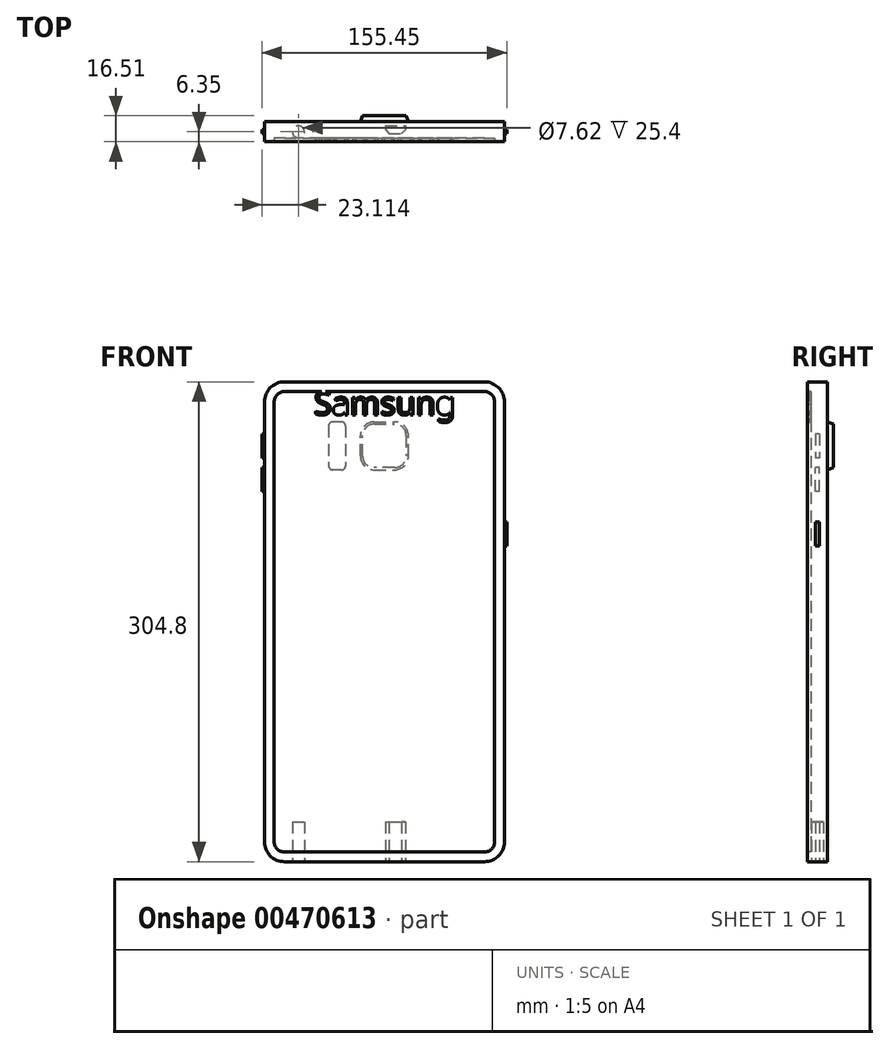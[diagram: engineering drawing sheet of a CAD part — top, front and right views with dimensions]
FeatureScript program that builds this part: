
annotation { "Feature Type Name" : "Feature", "Feature Type Description" : "" }
export const myFeature = defineFeature(function(context is Context, id is Id, definition is map)
    precondition{}
    {
        {
            var Q0;
            Q0=qCreatedBy(makeId("Front.planeOp"),FACE);
            var sketch = newSketch(context, id + "F0", { "sketchPlane" : qUnion([Q0])});
            skLineSegment(sketch, "E0.bottom", {"start": v(-70.4, 199.2) * mm, "end": v(56.6, 199.2) * mm});
            skLineSegment(sketch, "E0.top", {"start": v(-70.4, -105.6) * mm, "end": v(56.6, -105.6) * mm});
            skLineSegment(sketch, "E0.left", {"start": v(-83.1, 186.5) * mm, "end": v(-83.1, -92.9) * mm});
            skLineSegment(sketch, "E0.right", {"start": v(69.3, 186.5) * mm, "end": v(69.3, -92.9) * mm});
            skPoint(sketch, "E1.visualSharp", {"position": v(-83.1, 199.2) * mm});
            skArc(sketch, "E1.filletArc", {"start": v(-70.4, 199.2) * mm, "mid": v(-79.39, 195.48) * mm, "end": v(-83.1, 186.5) * mm});
            skPoint(sketch, "E2.visualSharp", {"position": v(69.3, 199.2) * mm});
            skArc(sketch, "E2.filletArc", {"start": v(69.3, 186.5) * mm, "mid": v(65.57, 195.48) * mm, "end": v(56.6, 199.2) * mm});
            skPoint(sketch, "E3.visualSharp", {"position": v(69.3, -105.6) * mm});
            skArc(sketch, "E3.filletArc", {"start": v(56.6, -105.6) * mm, "mid": v(65.57, -101.88) * mm, "end": v(69.3, -92.9) * mm});
            skPoint(sketch, "E4.visualSharp", {"position": v(-83.1, -105.6) * mm});
            skArc(sketch, "E4.filletArc", {"start": v(-83.1, -92.9) * mm, "mid": v(-79.39, -101.88) * mm, "end": v(-70.4, -105.6) * mm});
            skSolve(sketch);
        }
        {
            var Q0;
            Q0 = qSketchRegion(id + "F0", true);
            extrude(context, id + "F1", {"entities" : qUnion([Q0]), "depth" : 12.7 * mm});
        }
        {
            var Q0;
            Q0=makeQuery(id+"F1.opExtrude","SWEPT_FACE",FACE,{"disambiguationData":[OSD([sQuery(id+"F0.wireOp",EDGE,"E0.top")])]});
            var sketch = newSketch(context, id + "F2", { "sketchPlane" : qUnion([Q0])});
            skCircle(sketch, "E5", {"center": v(-61.52, 6.35) * mm, "radius": 3.81 * mm});
            skLineSegment(sketch, "E6.bottom", {"start": v(-6.35, 2.54) * mm, "end": v(6.35, 2.54) * mm});
            skLineSegment(sketch, "E6.top", {"start": v(-6.35, 7.62) * mm, "end": v(6.35, 7.62) * mm});
            skLineSegment(sketch, "E6.left", {"start": v(-6.35, 2.54) * mm, "end": v(-6.35, 7.62) * mm});
            skLineSegment(sketch, "E6.right", {"start": v(6.35, 2.54) * mm, "end": v(6.35, 7.62) * mm});
            skLineSegment(sketch, "E7", {"start": v(-6.35, 5.08) * mm, "end": v(-4.06, 7.62) * mm});
            skLineSegment(sketch, "E8.MirrorCS", {"start": v(6.35, 5.08) * mm, "end": v(4.06, 7.62) * mm});
            skLineSegment(sketch, "E9.0.0", {"start": v(-70.4, 0) * mm, "end": v(56.6, 0) * mm});
            skLineSegment(sketch, "E9.0.1", {"start": v(56.6, 0) * mm, "end": v(56.6, 12.7) * mm});
            skLineSegment(sketch, "E9.0.2", {"start": v(56.6, 12.7) * mm, "end": v(-70.4, 12.7) * mm});
            skLineSegment(sketch, "E9.0.3", {"start": v(-70.4, 12.7) * mm, "end": v(-70.4, 0) * mm});
            skSolve(sketch);
        }
        {
            var Q0;
            Q0=makeQuery(id+"F2.imprint","IMPRINT",FACE,{"disambiguationData":[TD([[makeQuery(id+"F2.imprint","IMPRINT",EDGE,{"derivedFrom":sQuery(id+"F2.wireOp",EDGE,"E5")}),1.0]])]});
            var Q1;
            {var subQ1=sQuery(id+"F2.wireOp",EDGE,"E6.bottom");Q1=makeQuery(id+"F2.imprint","IMPRINT",FACE,{"disambiguationData":[TD([[makeQuery(id+"F2.imprint","IMPRINT",EDGE,{"derivedFrom":subQ1}),1.0]])]});}
            extrude(context, id + "F3", {"entities" : qUnion([Q0, Q1]), "operationType" : NewBodyOperationType.REMOVE, "oppositeDirection" : true, "depth" : 25.4 * mm});
        }
        {
            var Q0;
            Q0=makeQuery(id+"F1.opExtrude","CAP_FACE",FACE,{"disambiguationData":[OSD([sQuery(id+"F0.wireOp",EDGE,"E0.bottom"),sQuery(id+"F0.wireOp",EDGE,"E0.top"),sQuery(id+"F0.wireOp",EDGE,"E0.left"),sQuery(id+"F0.wireOp",EDGE,"E0.right"),sQuery(id+"F0.wireOp",EDGE,"E1.filletArc"),sQuery(id+"F0.wireOp",EDGE,"E2.filletArc"),sQuery(id+"F0.wireOp",EDGE,"E3.filletArc"),sQuery(id+"F0.wireOp",EDGE,"E4.filletArc")])],"isStart":false});
            var sketch = newSketch(context, id + "F4", { "sketchPlane" : qUnion([Q0])});
            skLineSegment(sketch, "E10.0", {"start": v(-76.96, 186.5) * mm, "end": v(-76.96, -92.9) * mm});
            skArc(sketch, "E10.1", {"start": v(-70.4, 193.05) * mm, "mid": v(-75.04, 191.13) * mm, "end": v(-76.96, 186.5) * mm});
            skArc(sketch, "E10.2", {"start": v(-76.96, -92.9) * mm, "mid": v(-75.04, -97.54) * mm, "end": v(-70.4, -99.46) * mm});
            skLineSegment(sketch, "E10.3", {"start": v(56.6, 193.05) * mm, "end": v(-70.4, 193.05) * mm});
            skLineSegment(sketch, "E10.4", {"start": v(-70.4, -99.46) * mm, "end": v(56.6, -99.46) * mm});
            skArc(sketch, "E10.5", {"start": v(56.6, -99.46) * mm, "mid": v(61.23, -97.54) * mm, "end": v(63.15, -92.9) * mm});
            skLineSegment(sketch, "E10.6", {"start": v(63.15, -92.9) * mm, "end": v(63.15, 186.5) * mm});
            skArc(sketch, "E10.7", {"start": v(63.15, 186.5) * mm, "mid": v(61.23, 191.13) * mm, "end": v(56.6, 193.05) * mm});
            skText(sketch, "E11", { "text": "Samsung", "fontName": "NotoSans-Regular.ttf"});
            const initialGuessF4  = {"E11": [-0.05156, 0.17829, 1, 0, 0.01477]};
            skSetInitialGuess(sketch, initialGuessF4);
            skSolve(sketch);
        }
        {
            var Q0;
            Q0=makeQuery(id+"F4.imprint","IMPRINT",FACE,{"disambiguationData":[TD([[makeQuery(id+"F4.imprint","IMPRINT",EDGE,{"derivedFrom":sQuery(id+"F4.wireOp",EDGE,"E10.0")}),1.0]])]});
            extrude(context, id + "F5", {"entities" : qUnion([Q0]), "operationType" : NewBodyOperationType.REMOVE, "oppositeDirection" : true, "depth" : 2.3 * mm});
        }
        {
            var Q0;
            Q0=makeQuery(id+"F1.opExtrude","SWEPT_FACE",FACE,{"disambiguationData":[OSD([sQuery(id+"F0.wireOp",EDGE,"E0.left")])]});
            var sketch = newSketch(context, id + "F6", { "sketchPlane" : qUnion([Q0])});
            skLineSegment(sketch, "E12.bottom", {"start": v(5.08, 166.18) * mm, "end": v(7.62, 166.18) * mm});
            skLineSegment(sketch, "E12.top", {"start": v(5.08, 150.94) * mm, "end": v(7.62, 150.94) * mm});
            skLineSegment(sketch, "E12.left", {"start": v(5.08, 166.18) * mm, "end": v(5.08, 150.94) * mm});
            skLineSegment(sketch, "E12.right", {"start": v(7.62, 166.18) * mm, "end": v(7.62, 150.94) * mm});
            skLineSegment(sketch, "E13.MirrorCS", {"start": v(5.08, 129.47) * mm, "end": v(5.08, 144.7) * mm});
            skLineSegment(sketch, "E14.MirrorCS", {"start": v(7.62, 129.47) * mm, "end": v(7.62, 144.7) * mm});
            skLineSegment(sketch, "E15.MirrorCS", {"start": v(5.08, 144.7) * mm, "end": v(7.62, 144.7) * mm});
            skLineSegment(sketch, "E16.MirrorCS", {"start": v(5.08, 129.47) * mm, "end": v(7.62, 129.47) * mm});
            skSolve(sketch);
        }
        {
            var Q0;
            Q0=makeQuery(id+"F6.imprint","IMPRINT",FACE,{"disambiguationData":[TD([[makeQuery(id+"F6.imprint","IMPRINT",EDGE,{"derivedFrom":sQuery(id+"F6.wireOp",EDGE,"E12.bottom")}),-1.0]])]});
            var Q1;
            Q1=makeQuery(id+"F6.imprint","IMPRINT",FACE,{"disambiguationData":[TD([[makeQuery(id+"F6.imprint","IMPRINT",EDGE,{"derivedFrom":sQuery(id+"F6.wireOp",EDGE,"E13.MirrorCS")}),-1.0]])]});
            extrude(context, id + "F7", {"entities" : qUnion([Q0, Q1]), "operationType" : NewBodyOperationType.ADD, "depth" : 1.52 * mm});
        }
        {
            var Q0;
            Q0=makeQuery(id+"F1.opExtrude","SWEPT_FACE",FACE,{"disambiguationData":[OSD([sQuery(id+"F0.wireOp",EDGE,"E0.right")])]});
            var sketch = newSketch(context, id + "F8", { "sketchPlane" : qUnion([Q0])});
            skLineSegment(sketch, "E17.bottom", {"start": v(-7.62, 95.06) * mm, "end": v(-5.08, 95.06) * mm});
            skLineSegment(sketch, "E17.top", {"start": v(-7.62, 110.3) * mm, "end": v(-5.08, 110.3) * mm});
            skLineSegment(sketch, "E17.left", {"start": v(-7.62, 95.06) * mm, "end": v(-7.62, 110.3) * mm});
            skLineSegment(sketch, "E17.right", {"start": v(-5.08, 95.06) * mm, "end": v(-5.08, 110.3) * mm});
            skSolve(sketch);
        }
        {
            var Q0;
            Q0=makeQuery(id+"F8.imprint","IMPRINT",FACE,{"disambiguationData":[TD([[makeQuery(id+"F8.imprint","IMPRINT",EDGE,{"derivedFrom":sQuery(id+"F8.wireOp",EDGE,"E17.bottom")}),1.0]])]});
            extrude(context, id + "F9", {"entities" : qUnion([Q0]), "operationType" : NewBodyOperationType.ADD, "depth" : 1.52 * mm});
        }
        {
            var Q0;
            Q0=makeQuery(id+"F1.opExtrude","CAP_FACE",FACE,{"disambiguationData":[OSD([sQuery(id+"F0.wireOp",EDGE,"E0.bottom"),sQuery(id+"F0.wireOp",EDGE,"E0.top"),sQuery(id+"F0.wireOp",EDGE,"E0.left"),sQuery(id+"F0.wireOp",EDGE,"E0.right"),sQuery(id+"F0.wireOp",EDGE,"E1.filletArc"),sQuery(id+"F0.wireOp",EDGE,"E2.filletArc"),sQuery(id+"F0.wireOp",EDGE,"E3.filletArc"),sQuery(id+"F0.wireOp",EDGE,"E4.filletArc")])],"isStart":true});
            var sketch = newSketch(context, id + "F10", { "sketchPlane" : qUnion([Q0])});
            skLineSegment(sketch, "E18.bottom", {"start": v(13.37, 143.32) * mm, "end": v(0.45, 143.32) * mm});
            skLineSegment(sketch, "E18.top", {"start": v(13.37, 173.8) * mm, "end": v(0.45, 173.8) * mm});
            skLineSegment(sketch, "E18.left", {"start": v(22.15, 152.1) * mm, "end": v(22.15, 165.02) * mm});
            skLineSegment(sketch, "E18.right", {"start": v(-8.33, 152.1) * mm, "end": v(-8.33, 165.02) * mm});
            skPoint(sketch, "E18.middle", {"position": v(6.9, 158.56) * mm});
            skPoint(sketch, "E19.visualSharp", {"position": v(-8.33, 173.8) * mm});
            skArc(sketch, "E19.filletArc", {"start": v(0.45, 173.8) * mm, "mid": v(-5.76, 171.23) * mm, "end": v(-8.33, 165.02) * mm});
            skPoint(sketch, "E20.visualSharp", {"position": v(22.15, 173.8) * mm});
            skArc(sketch, "E20.filletArc", {"start": v(22.15, 165.02) * mm, "mid": v(19.57, 171.23) * mm, "end": v(13.37, 173.8) * mm});
            skPoint(sketch, "E21.visualSharp", {"position": v(22.15, 143.32) * mm});
            skArc(sketch, "E21.filletArc", {"start": v(13.37, 143.32) * mm, "mid": v(19.57, 145.89) * mm, "end": v(22.15, 152.1) * mm});
            skPoint(sketch, "E22.visualSharp", {"position": v(-8.33, 143.32) * mm});
            skArc(sketch, "E22.filletArc", {"start": v(-8.33, 152.1) * mm, "mid": v(-5.76, 145.89) * mm, "end": v(0.45, 143.32) * mm});
            skLineSegment(sketch, "E23.bottom", {"start": v(34.1, 173.8) * mm, "end": v(39.8, 173.8) * mm});
            skLineSegment(sketch, "E23.top", {"start": v(34.1, 143.32) * mm, "end": v(39.8, 143.32) * mm});
            skLineSegment(sketch, "E23.left", {"start": v(31.56, 171.26) * mm, "end": v(31.56, 145.86) * mm});
            skLineSegment(sketch, "E23.right", {"start": v(42.34, 171.26) * mm, "end": v(42.34, 145.86) * mm});
            skPoint(sketch, "E24.visualSharp", {"position": v(31.56, 173.8) * mm});
            skArc(sketch, "E24.filletArc", {"start": v(34.1, 173.8) * mm, "mid": v(32.3, 173.05) * mm, "end": v(31.56, 171.26) * mm});
            skPoint(sketch, "E25.visualSharp", {"position": v(42.34, 173.8) * mm});
            skArc(sketch, "E25.filletArc", {"start": v(42.34, 171.26) * mm, "mid": v(41.6, 173.05) * mm, "end": v(39.8, 173.8) * mm});
            skPoint(sketch, "E26.visualSharp", {"position": v(42.34, 143.32) * mm});
            skArc(sketch, "E26.filletArc", {"start": v(39.8, 143.32) * mm, "mid": v(41.6, 144.06) * mm, "end": v(42.34, 145.86) * mm});
            skPoint(sketch, "E27.visualSharp", {"position": v(31.56, 143.32) * mm});
            skArc(sketch, "E27.filletArc", {"start": v(31.56, 145.86) * mm, "mid": v(32.3, 144.06) * mm, "end": v(34.1, 143.32) * mm});
            skSolve(sketch);
        }
        {
            var Q0;
            Q0=makeQuery(id+"F10.imprint","IMPRINT",FACE,{"disambiguationData":[TD([[makeQuery(id+"F10.imprint","IMPRINT",EDGE,{"derivedFrom":sQuery(id+"F10.wireOp",EDGE,"E18.bottom")}),-1.0]])]});
            extrude(context, id + "F11", {"entities" : qUnion([Q0]), "operationType" : NewBodyOperationType.ADD, "depth" : 3.8 * mm});
        }
        {
            var Q0;
            Q0=makeQuery(id+"F11.opExtrude","CAP_FACE",FACE,{"disambiguationData":[OSD([sQuery(id+"F10.wireOp",EDGE,"E18.bottom"),sQuery(id+"F10.wireOp",EDGE,"E18.top"),sQuery(id+"F10.wireOp",EDGE,"E18.left"),sQuery(id+"F10.wireOp",EDGE,"E18.right"),sQuery(id+"F10.wireOp",EDGE,"E19.filletArc"),sQuery(id+"F10.wireOp",EDGE,"E20.filletArc"),sQuery(id+"F10.wireOp",EDGE,"E21.filletArc"),sQuery(id+"F10.wireOp",EDGE,"E22.filletArc")])],"isStart":false});
            chamfer(context, id + "F12", {"entities" : qUnion([Q0]), "chamferType" : ChamferType.OFFSET_ANGLE, "width" : 3.8 * mm, "oppositeDirection" : false, "angle" : 20 * degree, "tangentPropagation" : true});
        }
        {
            var Q0;
            Q0=makeQuery(id+"F10.imprint","IMPRINT",FACE,{"disambiguationData":[TD([[makeQuery(id+"F10.imprint","IMPRINT",EDGE,{"derivedFrom":sQuery(id+"F10.wireOp",EDGE,"E23.bottom")}),-1.0]])]});
            extrude(context, id + "F13", {"entities" : qUnion([Q0]), "operationType" : NewBodyOperationType.REMOVE, "oppositeDirection" : true, "depth" : 0.25 * mm});
        }
    });
